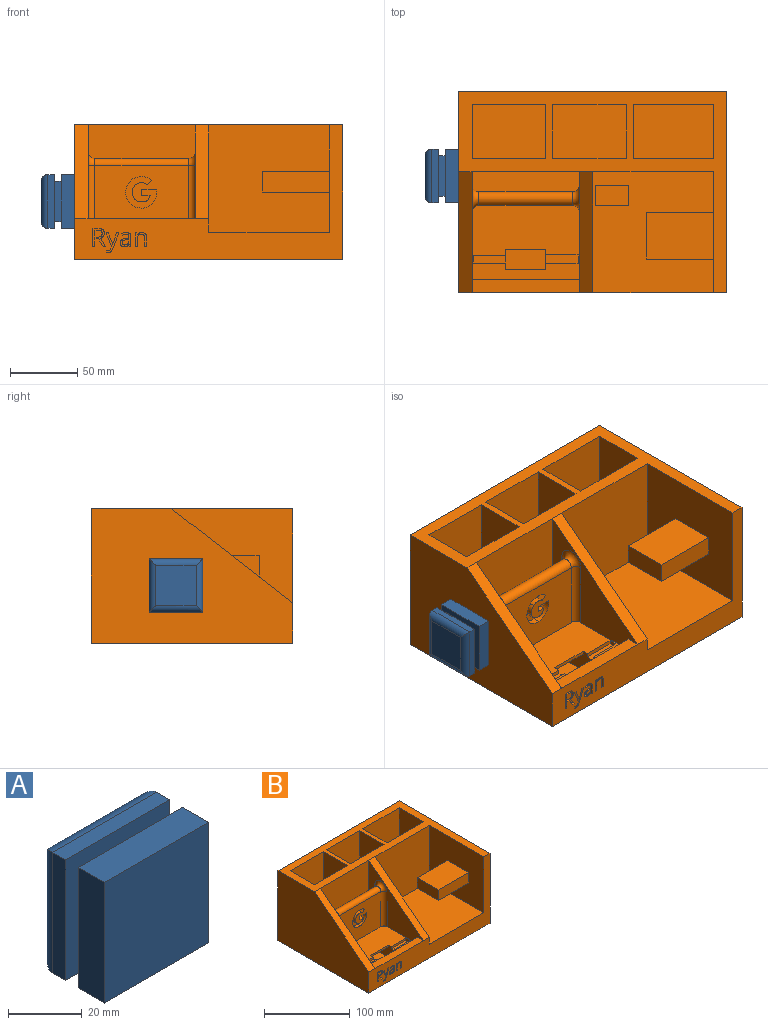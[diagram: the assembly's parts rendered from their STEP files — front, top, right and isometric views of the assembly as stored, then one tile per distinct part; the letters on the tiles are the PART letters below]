
ASSEMBLY  parts=2 mates=1
PART A: 20 faces, bbox 40x25x40 mm
  f0: plane 40x10mm, normal (0,0,-1), area 400mm2, adj f2,f4,f10,f12
  f1: plane 30x5mm, normal (1,0,0), area 150mm2, adj f3,f12,f13,f15
  f2: plane 40x10mm, normal (1,0,0), area 400mm2, adj f0,f9,f10,f12
  f3: plane 30x5mm, normal (0,0,1), area 150mm2, adj f1,f12,f13,f14
  f4: plane 40x10mm, normal (-1,0,0), area 400mm2, adj f0,f9,f10,f12
  f5: plane 40x5mm, normal (0,0,1), area 200mm2, adj f6,f8,f13,f18
  f6: plane 40x5mm, normal (-1,0,0), area 200mm2, adj f5,f7,f13,f16
  f7: plane 40x5mm, normal (0,0,-1), area 200mm2, adj f6,f8,f13,f17
  f8: plane 40x5mm, normal (1,0,0), area 200mm2, adj f5,f7,f13,f19
  f9: plane 40x10mm, normal (0,0,1), area 400mm2, adj f2,f4,f10,f12
  f10: plane 40x40mm, normal (0,-1,0), area 1600mm2, adj f0,f2,f4,f9
  f11: plane 30x30mm, normal (0,1,0), area 900mm2, adj f16,f17,f18,f19
  f12: plane 40x40mm, normal (0,1,0), area 700mm2, adj f0,f1,f2,f3,f4,f9,f14,f15
  f13: plane 40x40mm, normal (0,-1,0), area 700mm2, adj f1,f3,f5,f6,f7,f8,f14,f15
  f14: plane 30x5mm, normal (-1,0,0), area 150mm2, adj f3,f12,f13,f15
  f15: plane 30x5mm, normal (0,0,-1), area 150mm2, adj f1,f12,f13,f14
  f16: cylinder r=5mm len=40mm, axis (0,0,-1), area 285.6mm2, adj f6,f11,f17,f18
  f17: cylinder r=5mm len=40mm, axis (1,0,0), area 285.6mm2, adj f7,f11,f16,f19
  f18: cylinder r=5mm len=40mm, axis (-1,0,0), area 285.6mm2, adj f5,f11,f16,f19
  f19: cylinder r=5mm len=40mm, axis (0,0,1), area 285.6mm2, adj f8,f11,f17,f18
PART B: 166 faces, bbox 200x150x100 mm
  f0: plane 90x90mm, normal (0,0,1), area 7725mm2, adj f3,f21,f22,f23,f160,f161,f162,f163
  f1: plane 132.5x17.5mm, normal (1,0,0), area 2007.4mm2, adj f4,f20,f40,f42,f43,f44,f156,f158
  f2: plane 70x50mm, normal (0,-1,0), area 3223.5mm2, adj f20,f131,f134,f135,f138,f139,f140,f141
  f3: plane 200x100mm, normal (0,-1,0), area 5585.7mm2, adj f0,f5,f6,f7,f8,f21,f23,f34
  f4: plane 200x100mm, normal (0,1,0), area 19300mm2, adj f1,f5,f6,f7,f8,f40,f41,f42
  f5: plane 200x150mm, normal (0,0,1), area 6100mm2, adj f3,f4,f6,f8,f9,f10,f11,f12
  f6: plane 150x100mm, normal (-1,0,0), area 11850mm2, adj f3,f4,f5,f7,f45
  f7: plane 200x150mm, normal (0,0,-1), area 30000mm2, adj f3,f4,f6,f8
  f8: plane 150x100mm, normal (1,0,0), area 15000mm2, adj f3,f4,f5,f7
  f9: plane 80x40mm, normal (1,0,0), area 3200mm2, adj f5,f10,f12,f13
  f10: plane 80x55mm, normal (0,1,0), area 4400mm2, adj f5,f9,f11,f13
  f11: plane 80x40mm, normal (-1,0,0), area 3200mm2, adj f5,f10,f12,f13
  f12: plane 80x55mm, normal (0,-1,0), area 4400mm2, adj f5,f9,f11,f13
  f13: plane 55x40mm, normal (0,0,1), area 2200mm2, adj f9,f10,f11,f12
  f14: plane 80x80mm, normal (0,-1,0), area 6400mm2, adj f5,f16,f17,f19
  f15: plane 70x50mm, normal (0,1,0), area 3500mm2, adj f16,f132,f135,f137
  f16: plane 80x14.97mm, normal (0,0,1), area 1187.1mm2, adj f14,f15,f17,f19,f132,f137
  f17: plane 90x80mm, normal (1,0,0), area 2792.9mm2, adj f14,f16,f18,f20,f34,f45,f134,f136
  f18: plane 80x10mm, normal (0,1,0), area 800mm2, adj f17,f19,f20,f34
  f19: plane 90x80mm, normal (-1,0,0), area 2792.9mm2, adj f14,f16,f18,f20,f34,f130,f131,f132
  f20: plane 80x55.03mm, normal (0,0,1), area 3650.8mm2, adj f1,f2,f17,f18,f19,f41,f43,f44
  f21: plane 90x80mm, normal (-1,0,0), area 6675mm2, adj f0,f3,f5,f22,f35,f36,f37,f38
  f22: plane 90x80mm, normal (0,-1,0), area 7200mm2, adj f0,f5,f21,f23
  f23: plane 90x80mm, normal (1,0,0), area 4050mm2, adj f0,f3,f22,f130
  f24: plane 80x40mm, normal (1,0,0), area 3200mm2, adj f5,f25,f27,f28
  f25: plane 80x60mm, normal (0,1,0), area 4800mm2, adj f5,f24,f26,f28
  f26: plane 80x40mm, normal (-1,0,0), area 3200mm2, adj f5,f25,f27,f28
  f27: plane 80x60mm, normal (0,-1,0), area 4800mm2, adj f5,f24,f26,f28
  f28: plane 60x40mm, normal (0,0,1), area 2400mm2, adj f24,f25,f26,f27
  f29: plane 80x55mm, normal (0,-1,0), area 4400mm2, adj f5,f30,f32,f33
  f30: plane 80x40mm, normal (1,0,0), area 3200mm2, adj f5,f29,f31,f33
  f31: plane 80x55mm, normal (0,1,0), area 4400mm2, adj f5,f30,f32,f33
  f32: plane 80x40mm, normal (-1,0,0), area 3200mm2, adj f5,f29,f31,f33
  f33: plane 55x40mm, normal (0,0,1), area 2200mm2, adj f29,f30,f31,f32
  f34: plane 80x10mm, normal (0,0,1), area 800mm2, adj f3,f17,f18,f19
  f35: plane 50x35mm, normal (0,0,1), area 1750mm2, adj f21,f36,f38,f39
  f36: plane 50x15mm, normal (0,1,0), area 750mm2, adj f21,f35,f37,f39
  f37: plane 50x35mm, normal (0,0,-1), area 1750mm2, adj f21,f36,f38,f39
  f38: plane 50x15mm, normal (0,-1,0), area 750mm2, adj f21,f35,f37,f39
  f39: plane 35x15mm, normal (-1,0,0), area 525mm2, adj f35,f36,f37,f38
  f40: plane 117.5x30mm, normal (0,0,-1), area 3525mm2, adj f1,f4,f41,f44
  f41: plane 132.5x17.5mm, normal (-1,0,0), area 2006.2mm2, adj f4,f20,f40,f42,f43,f44,f153,f154
  f42: plane 132.5x30mm, normal (0,0,1), area 3975mm2, adj f1,f4,f41,f43
  f43: plane 30x17.5mm, normal (0,1,0), area 525mm2, adj f1,f20,f41,f42
  f44: plane 30x2.5mm, normal (0,-1,0), area 75mm2, adj f1,f20,f40,f41
  f45: plane 90x70mm, normal (0,-0.61,0.79), area 1140.2mm2, adj f3,f5,f6,f17
  f46: plane 5x1.65mm, normal (0,0,-1), area 8.3mm2, adj f3,f47,f61,f62
  f47: plane 10.22x5mm, normal (0.93,0,0.37), area 55.1mm2, adj f3,f46,f48,f62
  f48: plane 5x1.45mm, normal (0.93,0,-0.37), area 7.8mm2, adj f3,f47,f49,f62
  f49: extruded ~5x2.27mm, area 15.5mm2, adj f3,f48,f50,f62
  f50: extruded ~5x1.14mm, area 5.7mm2, adj f3,f49,f51,f62
  f51: plane 5x1.23mm, normal (1,0,0), area 6.2mm2, adj f3,f50,f52,f62
  f52: extruded ~5x1.39mm, area 7mm2, adj f3,f51,f53,f62
  f53: extruded ~5x2.13mm, area 11.5mm2, adj f3,f52,f54,f62
  f54: extruded ~5x2.44mm, area 14.5mm2, adj f3,f53,f55,f62
  f55: plane 11.58x5mm, normal (-0.94,0,0.35), area 61.9mm2, adj f3,f54,f56,f62
  f56: plane 5x1.65mm, normal (0,0,-1), area 8.3mm2, adj f3,f55,f57,f62
  f57: extruded ~7.05x5mm, area 37.4mm2, adj f3,f56,f58,f62
  f58: extruded ~5x1.62mm, area 8.5mm2, adj f3,f57,f59,f62
  f59: plane 5x0.07mm, normal (0,0,-1), area 0.4mm2, adj f3,f58,f60,f62
  f60: extruded ~5x2.87mm, area 15.1mm2, adj f3,f59,f61,f62
  f61: plane 5.8x5mm, normal (-0.93,0,-0.36), area 31.1mm2, adj f3,f46,f60,f62
  f62: plane 14.73x9.54mm, normal (0,-1,0), area 40.1mm2, adj f46,f47,f48,f49,f50,f51,f52,f53
  f63: extruded ~5x2.26mm, area 12.3mm2, adj f64,f89,f90,f128
  f64: extruded ~5x1.41mm, area 7.6mm2, adj f63,f65,f90,f128
  f65: extruded ~5x1.27mm, area 7.1mm2, adj f64,f66,f90,f128
  f66: extruded ~5x1.57mm, area 9.3mm2, adj f65,f67,f90,f128
  f67: extruded ~5x2.65mm, area 13.7mm2, adj f66,f68,f90,f128
  f68: plane 5x1.54mm, normal (-0.04,0,1), area 7.7mm2, adj f67,f69,f90,f128
  f69: plane 5x0.92mm, normal (1,0,0), area 4.6mm2, adj f68,f89,f90,f128
  f70: plane 5x1.45mm, normal (0.98,0,0.21), area 7.4mm2, adj f3,f71,f88,f90
  f71: plane 5x1.14mm, normal (0,0,1), area 5.7mm2, adj f3,f70,f72,f90
  f72: plane 6.94x5mm, normal (-1,0,0), area 34.7mm2, adj f3,f71,f73,f90
  f73: extruded ~5x2.59mm, area 14.1mm2, adj f3,f72,f74,f90
  f74: extruded ~5x2.69mm, area 14.4mm2, adj f3,f73,f75,f90
  f75: extruded ~5x1.8mm, area 9.1mm2, adj f3,f74,f76,f90
  f76: extruded ~5x1.65mm, area 8.8mm2, adj f3,f75,f77,f90
  f77: plane 5x1.18mm, normal (0.93,0,0.37), area 6.4mm2, adj f3,f76,f78,f90
  f78: extruded ~5x2.87mm, area 15mm2, adj f3,f77,f79,f90
  f79: extruded ~5x1.65mm, area 9mm2, adj f3,f78,f80,f90
  f80: extruded ~5x1.77mm, area 9.4mm2, adj f3,f79,f81,f90
  f81: plane 5x0.63mm, normal (1,0,0), area 3.2mm2, adj f3,f80,f82,f90
  f82: plane 5x1.73mm, normal (0.03,0,-1), area 8.6mm2, adj f3,f81,f83,f90
  f83: extruded ~5x4.93mm, area 33.1mm2, adj f3,f82,f84,f90
  f84: extruded ~5x2.22mm, area 12.3mm2, adj f3,f83,f85,f90
  f85: extruded ~5x2.37mm, area 12.8mm2, adj f3,f84,f86,f90
  f86: extruded ~5x1.89mm, area 9.7mm2, adj f3,f85,f87,f90
  f87: extruded ~5x1.52mm, area 10.1mm2, adj f3,f86,f88,f90
  f88: plane 5x0.07mm, normal (0,0,1), area 0.4mm2, adj f3,f70,f87,f90
  f89: extruded ~5x2.21mm, area 12.1mm2, adj f63,f69,f90,f128
  f90: plane 10.52x8.16mm, normal (0,-1,0), area 40.5mm2, adj f63,f64,f65,f66,f67,f68,f69,f70
  f91: plane 5x2.16mm, normal (0,0,-1), area 10.8mm2, adj f92,f108,f109,f129
  f92: plane 5.19x5mm, normal (-1,0,0), area 25.9mm2, adj f91,f93,f109,f129
  f93: plane 5x2.05mm, normal (0,0,1), area 10.3mm2, adj f92,f94,f109,f129
  f94: extruded ~5x2.55mm, area 13.3mm2, adj f93,f95,f109,f129
  f95: extruded ~5x1.94mm, area 10.9mm2, adj f94,f96,f109,f129
  f96: extruded ~5x1.99mm, area 11mm2, adj f95,f108,f109,f129
  f97: plane 5.64x5mm, normal (-1,0,0), area 28.2mm2, adj f3,f98,f107,f109
  f98: plane 5x2.83mm, normal (0,0,1), area 14.2mm2, adj f3,f97,f99,f109
  f99: plane 5.64x5mm, normal (0.86,0,0.5), area 32.6mm2, adj f3,f98,f100,f109
  f100: plane 5x1.86mm, normal (0,0,1), area 9.3mm2, adj f3,f99,f101,f109
  f101: plane 6.1x5mm, normal (-0.86,0,-0.52), area 35.6mm2, adj f3,f100,f102,f109
  f102: extruded ~5x3.64mm, area 24.5mm2, adj f3,f101,f103,f109
  f103: extruded ~5x2.88mm, area 16.1mm2, adj f3,f102,f104,f109
  f104: extruded ~5x3.69mm, area 19.4mm2, adj f3,f103,f105,f109
  f105: plane 5x3.72mm, normal (0,0,-1), area 18.6mm2, adj f3,f104,f106,f109
  f106: plane 13.56x5mm, normal (1,0,0), area 67.8mm2, adj f3,f105,f107,f109
  f107: plane 5x1.58mm, normal (0,0,1), area 7.9mm2, adj f3,f97,f106,f109
  f108: extruded ~5x2.45mm, area 12.9mm2, adj f91,f96,f109,f129
  f109: plane 13.56x9.56mm, normal (0,-1,0), area 55.2mm2, adj f91,f92,f93,f94,f95,f96,f97,f98
  f110: plane 6.58x5mm, normal (1,0,0), area 32.9mm2, adj f3,f111,f126,f127
  f111: plane 5x1.54mm, normal (0,0,1), area 7.7mm2, adj f3,f110,f112,f127
  f112: plane 6.63x5mm, normal (-1,0,0), area 33.2mm2, adj f3,f111,f113,f127
  f113: extruded ~5x2.84mm, area 15.3mm2, adj f3,f112,f114,f127
  f114: extruded ~5x2.77mm, area 14.9mm2, adj f3,f113,f115,f127
  f115: extruded ~5x1.9mm, area 9.8mm2, adj f3,f114,f116,f127
  f116: extruded ~5x1.33mm, area 9mm2, adj f3,f115,f117,f127
  f117: plane 5x0.07mm, normal (0,0,-1), area 0.4mm2, adj f3,f116,f118,f127
  f118: plane 5x1.39mm, normal (-0.98,0,-0.18), area 7.1mm2, adj f3,f117,f119,f127
  f119: plane 5x1.25mm, normal (0,0,-1), area 6.3mm2, adj f3,f118,f120,f127
  f120: plane 10.17x5mm, normal (1,0,0), area 50.8mm2, adj f3,f119,f121,f127
  f121: plane 5x1.54mm, normal (0,0,1), area 7.7mm2, adj f3,f120,f122,f127
  f122: plane 5.34x5mm, normal (-1,0,0), area 26.7mm2, adj f3,f121,f123,f127
  f123: extruded ~5x2.85mm, area 15mm2, adj f3,f122,f124,f127
  f124: extruded ~5x2.34mm, area 12.9mm2, adj f3,f123,f125,f127
  f125: extruded ~5x1.77mm, area 9.7mm2, adj f3,f124,f126,f127
  f126: extruded ~5x1.85mm, area 9.9mm2, adj f3,f110,f125,f127
  f127: plane 10.36x8.5mm, normal (0,-1,0), area 37.5mm2, adj f110,f111,f112,f113,f114,f115,f116,f117
  f128: plane 5x3.91mm, normal (0,-1,0), area 15.8mm2, adj f63,f64,f65,f66,f67,f68,f69,f89
  f129: plane 5.39x5.19mm, normal (0,-1,0), area 25.3mm2, adj f91,f92,f93,f94,f95,f96,f108
  f130: plane 90x70mm, normal (0,-0.61,0.79), area 1140.2mm2, adj f3,f5,f19,f23
  f131: cylinder r=5mm len=50mm, axis (0,0,-1), area 392.7mm2, adj f2,f19,f20,f133
  f132: cylinder r=5mm len=50mm, axis (0,0,1), area 392.7mm2, adj f15,f16,f19,f133
  f133: torus R=10mm, axis (-1,0,0), area 168.2mm2, adj f19,f131,f132,f135
  f134: cylinder r=5mm len=50mm, axis (0,0,1), area 392.7mm2, adj f2,f17,f20,f136
  f135: cylinder r=5mm len=70mm, axis (1,0,0), area 1099.6mm2, adj f2,f15,f133,f136
  f136: torus R=10mm, axis (-1,0,0), area 168.2mm2, adj f17,f134,f135,f137
  f137: cylinder r=5mm len=50mm, axis (0,0,-1), area 392.7mm2, adj f15,f16,f17,f136
  f138: plane 10.99x5mm, normal (0,0,-1), area 55mm2, adj f2,f139,f150,f151
  f139: plane 5x4.58mm, normal (1,0,0), area 22.9mm2, adj f2,f138,f140,f151
  f140: plane 6.23x5mm, normal (0,0,1), area 31.2mm2, adj f2,f139,f141,f151
  f141: cylinder r=5.68mm len=6.23mm, axis (0,-1,0), area 43.2mm2, adj f2,f140,f142,f151
  f142: cylinder r=6.46mm len=6.64mm, axis (0,-1,0), area 44.1mm2, adj f2,f141,f143,f151
  f143: cylinder r=6.77mm len=7.91mm, axis (0,-1,0), area 43.9mm2, adj f2,f142,f144,f151
  f144: cylinder r=6.87mm len=9.01mm, axis (0,-1,0), area 49.1mm2, adj f2,f143,f145,f151
  f145: plane 5x3.27mm, normal (-0.72,0,0.69), area 22.7mm2, adj f2,f144,f146,f151
  f146: cylinder r=11.23mm len=9.59mm, axis (0,-1,0), area 51.7mm2, adj f2,f145,f147,f151
  f147: cylinder r=10.88mm len=8.48mm, axis (0,-1,0), area 54.6mm2, adj f2,f146,f148,f151
  f148: cylinder r=11.56mm len=11.08mm, axis (0,-1,0), area 57.7mm2, adj f2,f147,f149,f151
  f149: cylinder r=11.67mm len=11.45mm, axis (0,-1,0), area 68.7mm2, adj f2,f148,f150,f151
  f150: cylinder r=11.38mm len=13.95mm, axis (0,-1,0), area 97.3mm2, adj f2,f138,f149,f151
  f151: plane 23.56x23.16mm, normal (0,-1,0), area 276.5mm2, adj f138,f139,f140,f141,f142,f143,f144,f145
  f152: plane 6.25x3mm, normal (-1,0,0), area 18.8mm2, adj f20,f153,f154,f155
  f153: plane 24x3mm, normal (0,-1,0), area 72mm2, adj f20,f41,f152,f155
  f154: plane 24x3mm, normal (0,1,0), area 72mm2, adj f20,f41,f152,f155
  f155: plane 24x6.25mm, normal (0,0,1), area 150mm2, adj f41,f152,f153,f154
  f156: plane 24x3mm, normal (0,-1,0), area 72mm2, adj f1,f20,f157,f159
  f157: plane 5.86x3mm, normal (1,0,0), area 17.6mm2, adj f20,f156,f158,f159
  f158: plane 24x3mm, normal (0,1,0), area 72mm2, adj f1,f20,f157,f159
  f159: plane 24x5.86mm, normal (0,0,1), area 140.6mm2, adj f1,f156,f157,f158
  f160: plane 25x5mm, normal (0,-1,0), area 125mm2, adj f0,f161,f163,f165
  f161: plane 85x15mm, normal (1,0,0), area 925mm2, adj f0,f4,f160,f162,f164,f165
  f162: plane 25x15mm, normal (0,1,0), area 375mm2, adj f0,f161,f163,f164
  f163: plane 85x15mm, normal (-1,0,0), area 925mm2, adj f0,f4,f160,f162,f164,f165
  f164: plane 85x25mm, normal (0,0,1), area 2125mm2, adj f4,f161,f162,f163
  f165: plane 70x25mm, normal (0,0,-1), area 1750mm2, adj f4,f160,f161,f163
PLACE A rot(axis=(0.58,-0.58,0.58),120deg) t=(-62.44,59.2,-40.41)mm
PLACE B t=(-37.44,102.24,-63.32)mm
MATE fastened A.f10 <-> B.f6  axis (1,0,0) through (-37.44,39.2,-20.41)mm
